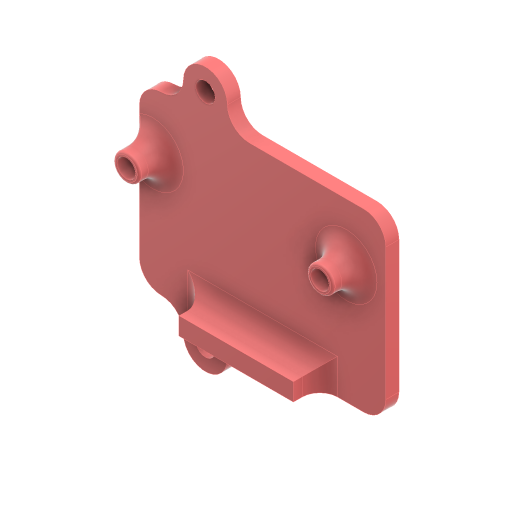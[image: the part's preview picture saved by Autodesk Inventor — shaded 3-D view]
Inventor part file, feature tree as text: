
AUTODESK INVENTOR PART (.ipt)
format: ipt  version: 2023 (Build 270158000, 158)  size: 245,248 bytes
history: native  units: mm
features: extrude x3, fillet x3, sketch x2
ambient origin geometry x8: Origin, YZ Plane, XZ Plane, XY Plane, X Axis, Y Axis, Z Axis, Center Point
bodies: Solid1 (feature_tree)
feature tree (8):
  sketch  "Sketch1"  dims[d0=56.0mm d1=40.0mm]
  extrude  "Extrusion1"  Depth=56.0mm
  extrude  "Extrusion2"  Depth=5.0mm
  fillet  "Fillet1"  Radius=27.0mm
  fillet  "Fillet2"  Radius=27.0mm
  extrude  "Extrusion3"  Depth=3.0mm
  fillet  "Fillet3"  Radius=47.0mm
  sketch  "Sketch2"  dims[d2=4.2mm d3=4.2mm d4=27.0mm d5=27.0mm d6=3.0mm d7=47.0mm d8=6.0mm d9=6.0mm d10=4.0mm d11=15.0mm d12=15.0mm d13=3.0mm d14=0.0mm d15=6.0mm d16=0.0mm d17=4.0mm d18=0.5mm d19=4.4mm d20=4.4mm d21=50.0mm d22=25.0mm d23=15.0mm d24=10.0mm d25=3.0mm d26=0.0mm d27=5.0mm]
